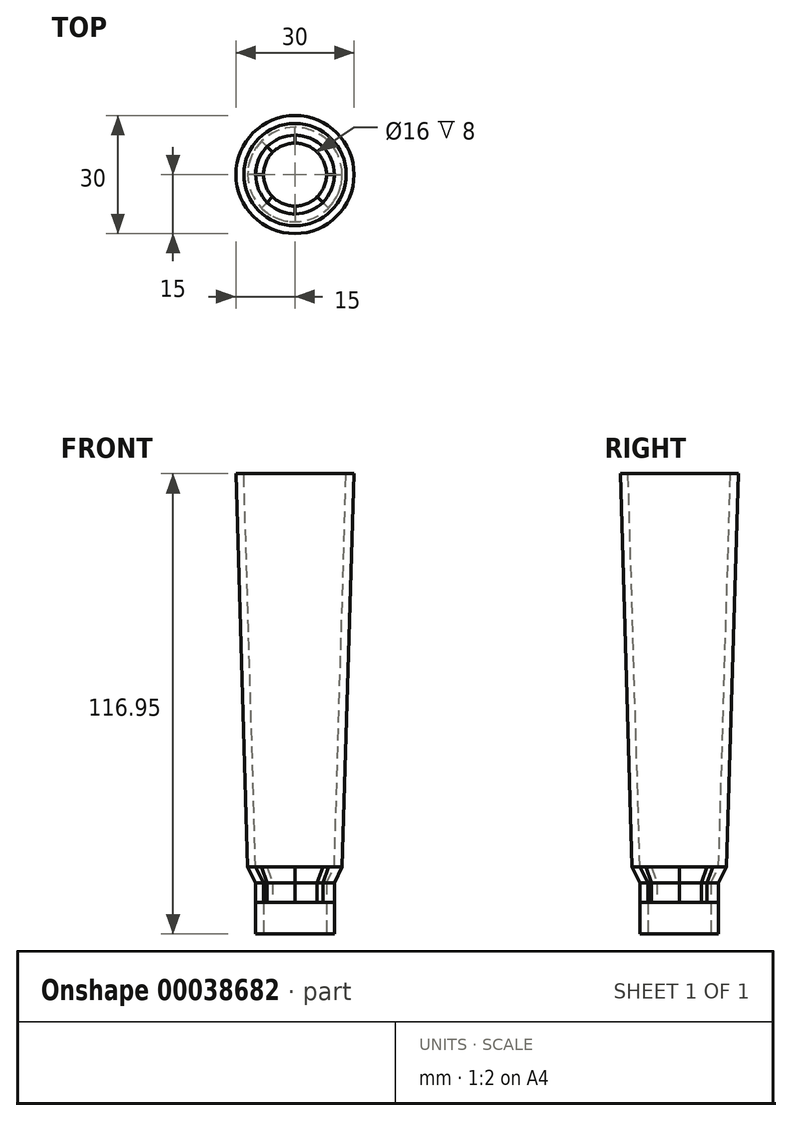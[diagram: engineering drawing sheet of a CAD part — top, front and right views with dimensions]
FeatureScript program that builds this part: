
annotation { "Feature Type Name" : "Feature", "Feature Type Description" : "" }
export const myFeature = defineFeature(function(context is Context, id is Id, definition is map)
    precondition{}
    {
        {
            var Q0;
            Q0=qCreatedBy(makeId("Top.planeOp"),FACE);
            var sketch = newSketch(context, id + "F0", { "sketchPlane" : qUnion([Q0])});
            skCircle(sketch, "E0", {"center": v(0, 0) * mm, "radius": 10 * mm});
            skCircle(sketch, "E1", {"center": v(0, 0) * mm, "radius": 8 * mm});
            skSolve(sketch);
        }
        {
            var Q0;
            Q0=makeQuery(id+"F0.imprint","IMPRINT",FACE,{"disambiguationData":[TD([[makeQuery(id+"F0.imprint","IMPRINT",EDGE,{"derivedFrom":sQuery(id+"F0.wireOp",EDGE,"E0")}),1.0]])]});
            extrude(context, id + "F1", {"entities" : qUnion([Q0]), "depth" : 8 * mm});
        }
        {
            var Q0;
            Q0=makeQuery(id+"F1.opExtrude","CAP_FACE",FACE,{"disambiguationData":[OSD([sQuery(id+"F0.wireOp",EDGE,"E0"),sQuery(id+"F0.wireOp",EDGE,"E1")])],"isStart":false});
            var sketch = newSketch(context, id + "F2", { "sketchPlane" : qUnion([Q0])});
            skLineSegment(sketch, "E2", {"start": v(0, 10) * mm, "end": v(0, 8) * mm});
            skLineSegment(sketch, "E3", {"start": v(5.66, 5.66) * mm, "end": v(7.07, 7.07) * mm});
            skSolve(sketch);
        }
        {
            var Q0;
            {var subQ2=sQuery(id+"F2.wireOp",EDGE,"E2");Q0=makeQuery(id+"F2.imprint","IMPRINT",FACE,{"disambiguationData":[TD([[makeQuery(id+"F2.imprint","IMPRINT",EDGE,{"derivedFrom":subQ2}),1.0]])]});}
            extrude(context, id + "F3", {"entities" : qUnion([Q0]), "depth" : 5 * mm});
        }
        {
            var Q0;
            Q0=makeQuery(id+"F3.opExtrude","SWEPT_BODY",BODY,{"disambiguationData":[OSD([sQuery(id+"F0.wireOp",EDGE,"E0"),sQuery(id+"F0.wireOp",EDGE,"E1"),sQuery(id+"F2.wireOp",EDGE,"E2"),sQuery(id+"F2.wireOp",EDGE,"E3")])]});
            var Q1;
            Q1=makeQuery(id+"F1.opExtrude","CAP_EDGE",EDGE,{"disambiguationData":[OSD([sQuery(id+"F0.wireOp",EDGE,"E1")])],"isStart":false});
            circularPattern(context, id + "F4", {"entities" : qUnion([Q0]), "axis" : qUnion([Q1]), "angle" : 90 * degree, "instanceCount" : 4});
        }
        {
            var Q0;
            Q0=makeQuery(id+"F3.opExtrude","SWEPT_FACE",FACE,{"disambiguationData":[OSD([sQuery(id+"F2.wireOp",EDGE,"E2")])]});
            var sketch = newSketch(context, id + "F5", { "sketchPlane" : qUnion([Q0])});
            skLineSegment(sketch, "E4", {"start": v(-10, 13) * mm, "end": v(-12, 17) * mm});
            skLineSegment(sketch, "E5", {"start": v(-8, 13) * mm, "end": v(-10, 17) * mm});
            skLineSegment(sketch, "E6", {"start": v(-10, 17) * mm, "end": v(-12, 17) * mm});
            skSolve(sketch);
        }
        {
            var Q0;
            Q0=makeQuery(id+"F5.imprint","IMPRINT",FACE,{"disambiguationData":[TD([[makeQuery(id+"F5.imprint","IMPRINT",EDGE,{"derivedFrom":sQuery(id+"F5.wireOp",EDGE,"E4")}),-1.0]])]});
            var Q1;
            Q1=makeQuery(id+"F1.opExtrude","CAP_EDGE",EDGE,{"disambiguationData":[OSD([sQuery(id+"F0.wireOp",EDGE,"E1")])],"isStart":false});
            revolve(context, id + "F6", {"entities" : qUnion([Q0]), "axis" : qUnion([Q1]), "revolveType" : RevolveType.FULL});
        }
        {
            var Q0;
            Q0=makeQuery(id+"F3.opExtrude","CAP_FACE",FACE,{"disambiguationData":[OSD([sQuery(id+"F0.wireOp",EDGE,"E0"),sQuery(id+"F0.wireOp",EDGE,"E1"),sQuery(id+"F2.wireOp",EDGE,"E2"),sQuery(id+"F2.wireOp",EDGE,"E3")])],"isStart":false});
            var sketch = newSketch(context, id + "F7", { "sketchPlane" : qUnion([Q0])});
            skLineSegment(sketch, "E7", {"start": v(0, 10) * mm, "end": v(0, 0) * mm});
            skLineSegment(sketch, "E8", {"start": v(0, 0) * mm, "end": v(-7.07, 7.07) * mm});
            skLineSegment(sketch, "E9", {"start": v(-7.07, 7.07) * mm, "end": v(-11.2, 11.2) * mm});
            skLineSegment(sketch, "E10", {"start": v(-11.2, 11.2) * mm, "end": v(0, 15.02) * mm});
            skLineSegment(sketch, "E11", {"start": v(0, 15.02) * mm, "end": v(0, 10) * mm});
            skSolve(sketch);
        }
        {
            var Q0;
            {var subQ2=sQuery(id+"F7.wireOp",EDGE,"E8");Q0=makeQuery(id+"F7.imprint","IMPRINT",FACE,{"disambiguationData":[TD([[makeQuery(id+"F7.imprint","IMPRINT",EDGE,{"derivedFrom":subQ2}),-1.0]])]});}
            var Q1;
            Q1=makeQuery(id+"F6.opRevolve","SWEPT_FACE",FACE,{"disambiguationData":[OSD([sQuery(id+"F5.wireOp",EDGE,"E6")])]});
            extrude(context, id + "F8", {"entities" : qUnion([Q0]), "endBound" : BoundingType.UP_TO_SURFACE, "endBoundEntityFace" : qUnion([Q1]), "depth" : 25 * mm});
        }
        {
            var Q0;
            Q0=makeQuery(id+"F8.opExtrude","SWEPT_BODY",BODY,{"disambiguationData":[OSD([sQuery(id+"F7.wireOp",EDGE,"E7"),sQuery(id+"F7.wireOp",EDGE,"E8"),sQuery(id+"F7.wireOp",EDGE,"E9"),sQuery(id+"F7.wireOp",EDGE,"E10"),sQuery(id+"F7.wireOp",EDGE,"E11")])]});
            var Q1;
            Q1=makeQuery(id+"F1.opExtrude","CAP_EDGE",EDGE,{"disambiguationData":[OSD([sQuery(id+"F0.wireOp",EDGE,"E1")])],"isStart":false});
            circularPattern(context, id + "F9", {"entities" : qUnion([Q0]), "axis" : qUnion([Q1]), "angle" : 90 * degree, "instanceCount" : 4});
        }
        {
            var Q0;
            Q0=makeQuery(id+"F8.opExtrude","SWEPT_BODY",BODY,{"disambiguationData":[OSD([sQuery(id+"F7.wireOp",EDGE,"E7"),sQuery(id+"F7.wireOp",EDGE,"E8"),sQuery(id+"F7.wireOp",EDGE,"E9"),sQuery(id+"F7.wireOp",EDGE,"E10"),sQuery(id+"F7.wireOp",EDGE,"E11")])]});
            var Q1;
            Q1=makeQuery(id+"F9.opPattern","COPY",BODY,{"derivedFrom":makeQuery(id+"F8.opExtrude","SWEPT_BODY",BODY,{"disambiguationData":[OSD([sQuery(id+"F7.wireOp",EDGE,"E7"),sQuery(id+"F7.wireOp",EDGE,"E8"),sQuery(id+"F7.wireOp",EDGE,"E9"),sQuery(id+"F7.wireOp",EDGE,"E10"),sQuery(id+"F7.wireOp",EDGE,"E11")])]}),"instanceName":"3"});
            var Q2;
            Q2=makeQuery(id+"F9.opPattern","COPY",BODY,{"derivedFrom":makeQuery(id+"F8.opExtrude","SWEPT_BODY",BODY,{"disambiguationData":[OSD([sQuery(id+"F7.wireOp",EDGE,"E7"),sQuery(id+"F7.wireOp",EDGE,"E8"),sQuery(id+"F7.wireOp",EDGE,"E9"),sQuery(id+"F7.wireOp",EDGE,"E10"),sQuery(id+"F7.wireOp",EDGE,"E11")])]}),"instanceName":"2"});
            var Q3;
            Q3=makeQuery(id+"F9.opPattern","COPY",BODY,{"derivedFrom":makeQuery(id+"F8.opExtrude","SWEPT_BODY",BODY,{"disambiguationData":[OSD([sQuery(id+"F7.wireOp",EDGE,"E7"),sQuery(id+"F7.wireOp",EDGE,"E8"),sQuery(id+"F7.wireOp",EDGE,"E9"),sQuery(id+"F7.wireOp",EDGE,"E10"),sQuery(id+"F7.wireOp",EDGE,"E11")])]}),"instanceName":"1"});
            var Q4;
            Q4=makeQuery(id+"F6.opRevolve","SWEPT_BODY",BODY,{"disambiguationData":[OSD([sQuery(id+"F2.wireOp",EDGE,"E2"),sQuery(id+"F5.wireOp",EDGE,"E4"),sQuery(id+"F5.wireOp",EDGE,"E5"),sQuery(id+"F5.wireOp",EDGE,"E6")])]});
            booleanBodies(context, id + "F10", {"operationType" : BooleanOperationType.SUBTRACTION, "tools" : qUnion([Q0, Q1, Q2, Q3]), "targets" : qUnion([Q4])});
        }
        {
            var Q0;
            Q0=makeQuery(id+"F10.opBoolean","COPY",FACE,{"derivedFrom":makeQuery(id+"F9.opPattern","COPY",FACE,{"derivedFrom":makeQuery(id+"F8.opExtrude","SWEPT_FACE",FACE,{"disambiguationData":[OSD([sQuery(id+"F7.wireOp",EDGE,"E7"),sQuery(id+"F7.wireOp",EDGE,"E11")])]}),"instanceName":"3"})});
            var sketch = newSketch(context, id + "F11", { "sketchPlane" : qUnion([Q0])});
            skLineSegment(sketch, "E12", {"start": v(-12, 17) * mm, "end": v(-15, 116.95) * mm});
            skLineSegment(sketch, "E13", {"start": v(-15, 116.95) * mm, "end": v(-13, 116.95) * mm});
            skLineSegment(sketch, "E14", {"start": v(-13, 116.95) * mm, "end": v(-10, 17) * mm});
            skSolve(sketch);
        }
        {
            var Q0;
            Q0=makeQuery(id+"F11.imprint","IMPRINT",FACE,{"disambiguationData":[TD([[makeQuery(id+"F11.imprint","IMPRINT",EDGE,{"derivedFrom":sQuery(id+"F11.wireOp",EDGE,"E12")}),-1.0]])]});
            var Q1;
            Q1=makeQuery(id+"F1.opExtrude","CAP_EDGE",EDGE,{"disambiguationData":[OSD([sQuery(id+"F0.wireOp",EDGE,"E1")])],"isStart":false});
            revolve(context, id + "F12", {"entities" : qUnion([Q0]), "axis" : qUnion([Q1]), "revolveType" : RevolveType.FULL});
        }
    });
